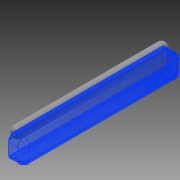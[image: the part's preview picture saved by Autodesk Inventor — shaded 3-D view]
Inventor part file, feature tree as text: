
AUTODESK INVENTOR PART (.ipt)
format: ipt  version: 2014 SP1 (Build 180222100, 222)  size: 86,528 bytes
history: native  units: in
note: dims shown in document units (in); Inventor stores cm internally (conversion verified against a paired STEP export)
features: extrude x1, fillet x1, sketch x1
ambient origin geometry x8: Origin, YZ Plane, XZ Plane, XY Plane, X Axis, Y Axis, Z Axis, Center Point
bodies: Solid1 (feature_tree)
feature tree (3):
  extrude  "Extrusion1"  Depth=1.0in
  fillet  "Fillet1"  Radius=33.375in
  sketch  "Sketch1"  dims[d0=2.5in d1=0.75in d2=33.375in d3=0.0in d4=1.0in]
